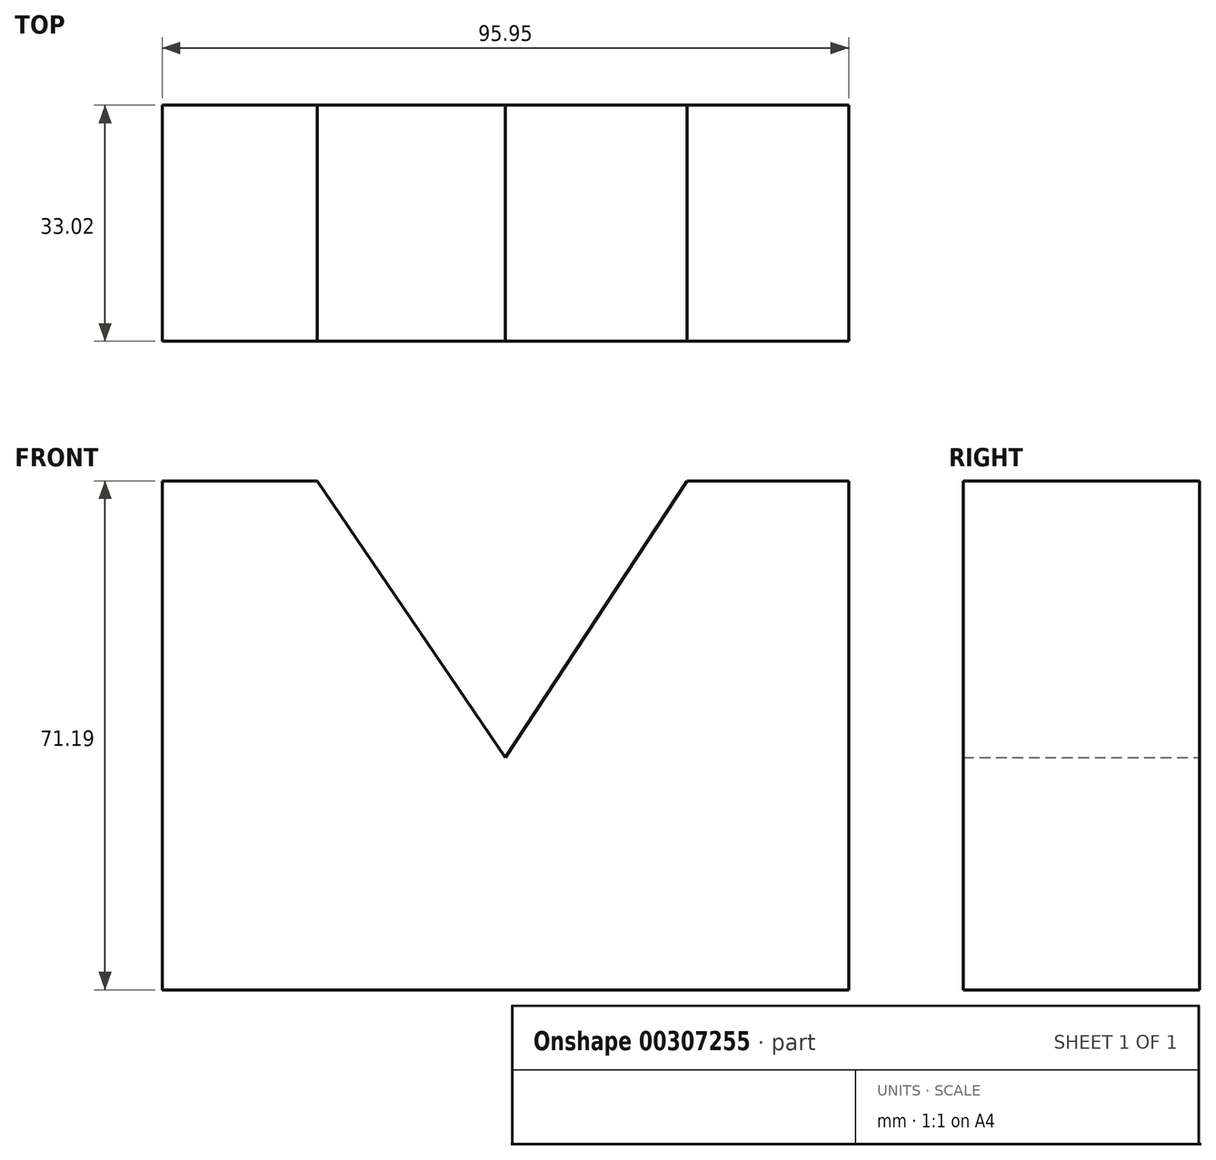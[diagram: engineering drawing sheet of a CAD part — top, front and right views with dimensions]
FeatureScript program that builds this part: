
annotation { "Feature Type Name" : "Feature", "Feature Type Description" : "" }
export const myFeature = defineFeature(function(context is Context, id is Id, definition is map)
    precondition{}
    {
        {
            var Q0;
            Q0=qCreatedBy(makeId("Front.planeOp"),FACE);
            var sketch = newSketch(context, id + "F0", { "sketchPlane" : qUnion([Q0])});
            skLineSegment(sketch, "E0", {"start": v(-44.26, -47.2) * mm, "end": v(51.69, -47.2) * mm});
            skLineSegment(sketch, "E1", {"start": v(51.69, -47.2) * mm, "end": v(51.69, 23.99) * mm});
            skLineSegment(sketch, "E2", {"start": v(51.69, 23.99) * mm, "end": v(29.1, 23.99) * mm});
            skLineSegment(sketch, "E3", {"start": v(-44.26, -47.2) * mm, "end": v(-44.26, 23.99) * mm});
            skLineSegment(sketch, "E4", {"start": v(3.71, -14.7) * mm, "end": v(29.1, 23.99) * mm});
            skPoint(sketch, "E4.startSnap0", {"position": v(3.71, -47.2) * mm});
            skLineSegment(sketch, "E5", {"start": v(-22.6, 23.99) * mm, "end": v(3.71, -14.7) * mm});
            skLineSegment(sketch, "E6", {"start": v(-22.6, 23.99) * mm, "end": v(-44.26, 23.99) * mm});
            skSolve(sketch);
        }
        {
            var Q0;
            Q0=makeQuery(id+"F0.imprint","IMPRINT",FACE,{"disambiguationData":[TD([[makeQuery(id+"F0.imprint","IMPRINT",EDGE,{"derivedFrom":sQuery(id+"F0.wireOp",EDGE,"E0")}),1.0]])]});
            extrude(context, id + "F1", {"entities" : qUnion([Q0]), "depth" : 33.02 * mm});
        }
    });
